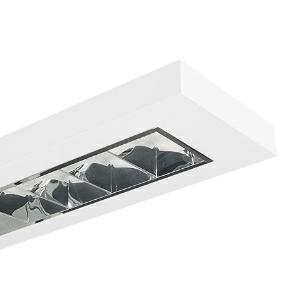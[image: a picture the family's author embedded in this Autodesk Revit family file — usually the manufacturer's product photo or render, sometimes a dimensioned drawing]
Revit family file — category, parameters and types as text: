
# Revit family: 3f_filippi_-_3f_travetta_2mg_3f_filippi_-_11515_-_3f_travetta_led_1x30w-940_dali_2mg_l1590
name_source: partatom
category: Lighting Fixtures
units: mm (PartAtom-declared; Revit-internal decimal feet)

## family parameters
Cut with Voids When Loaded = No
Host = Face
Light Source = No
Part Type = Normal
Room Calculation Point = No
Round Connector Dimension = Use Diameter
Shared = No

## types (1)
- 3F Filippi - 3F Travetta 2MG (1 x LED, 3084 lm, 34 W, 4000 K)
    Apparent Load = 34 VA
    Approval mark = ENEC
    CIE Flux Codes = 72 99 100 100 100
    Color Rendering = 90
    Color Temperature = 4000 K
    Control Gear = Electronic transformer
    Default Elevation = 1800 mm
    Description = ILLUMINOTECHNICAL
Luminous efficiency 100% (DLOR 100%, ULOR 0%).
Initial luminous flux of the luminaire 3084 lm.
Direct symmetric distribution.
Installation Interdistance Transv.D = 1.49 x hu - Long.D = 1.23 x hu.
Average luminance <1000 cd/m² for radial angles >65°.
Tabular UGR (CIE 117 - 4H-8H; S=0.25H; 70/50/20): RUG 14.8 - 17.
Beam angle: 80° - 82°.
Luminous efficacy 91 lm/W.
Lifetime (L93/B10): 30000 h. (tq+25°C)
Lifetime (L90/B10): 50000 h. (tq+25°C)
Lifetime (L85/B10): 80000 h. (tq+25°C)
Lifetime (L80/B10): 100000 h. (tq+25°C)
Sudden decreased luminous flux after 50000 hours: 0% (C0).
Photobiological safety in compliance with IEC/TR 62778: RG0 risk exempt, (IEC 62471).
In compliance with IEC/EN 62722-2-1 - IEC/EN 62717 standards.

SOURCE
Linear LED module 30W/940.
Energy efficiency class (UE 2019/2020 - UE 2019/2015): E.
CIE 13.3 Colour rendering index: CRI >90 (R9 >50%).
IES TM-30 Fidelity Index: Rf = 92 Rg = 101.
CCT nominal colour temperature 4000 K.
Colour initial tolerance (MacAdam): SDCM 2.

MECHANICAL
Housing with squared shape in white painted galvannealed steel, with nonreflecting surface.
2MG parabolic louvre, high efficiency, in specular aluminium with superficial titanium-magnesium treatment, non-iridescent, with transverse blades closed at the top.
Prismatic flat diffuser in transparent methacrylate (PMMA), multilenticular, anti-glare, prismatic exterior, placed above louvre blades.
Film protective against dust and finger marks, adhesive, attached to louvre.
Luminaire with limited surface temperature. - D - (EN 60598-2-24)
Dimensions: 1590x190 mm, height 60 mm. Weight 5.06 kg.
IP20 protection degree.
Mechanical strength to impacts IK02 (0.2 joule).
Glow-wire test resistance 650°C.

ELECTRICAL
Halogen Free DALI-2 DATI (Parts 251, 252, 253), PUSH-DIM, electronic wiring 230V-50/60Hz, power factor 0.95 at full load, THD <25%, constant output current, SELV, class I, 1 driver, 1 DALI addresse.
Power of the luminaire 34 W.
CE - IEC 60598-1 - EN 60598-1.
SAFE FLICKER: PstLM=<1 and SVM=<0.4 (IEC TR 61547-1 and IEC TR 63158), to ensure a more comfortable and safe light.
Luminaire compliant with EN 60598-2-22 for power supply from a centralised emergency system CPSS (Central Power Supply System), not incorporated in the luminaire - high risk areas excluded. The default power and flux are 100% in AC and 15% in DC.
Ambient temperature from 0°C to +25°C.
Temperature class T6 max 85°C.
5-pole terminal block for cascade line connection with connection capacity 2x2.5 mm².
Relative humidity UR: <85%.

INSTALLATION
Ceiling / Suspended.
All accessories dedicated to this product are available on the Catalog and on our website www.3F-Filippi.com.

APPLICATIONS
In environments, even with reduced height, requiring a comfortable light.
Exhibitions area, halls, great halls and shops.
In environments with VDTs, managerial offices and staterooms, public offices and schools.

LIGHT MANAGEMENT
Recommended minimum setting: 10%.
The luminaire, equipped with (DALI-2 DATI) driver, can be controlled manually with 3F Easy Dim technology or automatically/manually with wired or wireless DALI/D2D control systems.
The D2D driver guarantees interoperability with other devices with the same certification by making the following information available:
Device Data (Part 251), Energy Report (Part 252), Diagnosis & Maintenance (Part 253).
In electrical systems without a regulation system (manual or automatic) and DALI bus, a suitable jumper must be made on the DA-DA terminals of the appliance.

WARNING
Luminaire designed for disposal/recycling at end-of-life.
Replaceable (LED only) light source by a professional. Replaceable control gear by a professional.
    Height = 60 mm  [stored 0.19685 ft]
    Lamp = 1 x LED
    Lamp Light Flux = 3084 lm
    Lamp Power = 34 W
    Lamp count = 1
    Length = 1590 mm
    Lifetime = 50000 h
    Luminous efficacy = 91 lm/W
    Manufacturer = 3F Filippi
    ModVariant = No
    Model = 3F Filippi - 11515 - 3F Travetta LED 1x30W-940 DALI 2MG L1590
    Mounting Place = Ceiling
    Mounting Type = Pendant
    Number of Poles = 1
    OnlyDefault = Yes
    Power Factor = 1
    Product Name = 3F Filippi - 3F Travetta 2MG
    Product group = pendant luminaire
    ProductGroupID = 9
    Protection Class = Protection class I
    Protection Degree = IP 20
    RLX_Detail_Level = 1
    RLX_Emergency_Light_Flux = 0 lm
    RLX_Emergency_Type = 0
    RLX_Emergency_Type_DB = No
    RlxData = <blob elided: 57461 chars, md5=356e0714>
    Socket = socket
    Standby Power = 0 W
    System Light Flux = 3084 lm
    System Power = 34 W
    Type Comments = Product without accessories
    Type Image = 3ffilippi_3f_travetta_led_2mg.jpg
    URL = http://relux.com
    VarID = ---
    Voltage = 0 V
    Weight = 0.00 kg
    Width = 190 mm  [stored 0.62336 ft]

note: [stored X ft] marks values corroborated as IEEE doubles in the binary element streams (Revit-internal decimal feet)

## geometry (parser evidence)
native form markers: Blend x4, Sweep x11
no freeform markers — native parametric forms only
